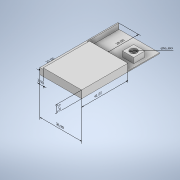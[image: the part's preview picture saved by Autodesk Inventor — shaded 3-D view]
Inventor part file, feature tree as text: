
AUTODESK INVENTOR PART (.ipt)
format: ipt  version: 2020 (Build 240168000, 168)  size: 172,032 bytes
history: native  units: mm
features: other x8, sketch x7, extrude x5, hole x1
ambient origin geometry x8: Origin, YZ Plane, XZ Plane, XY Plane, X Axis, Y Axis, Z Axis, Center Point
bodies: Solid1 (feature_tree)
feature tree (21):
  other  "Annotations"
  extrude  "Extrusion1"  Depth=69.0mm
  extrude  "Extrusion2"  Depth=34.0mm
  sketch  "Sketch4"  dims[d5=41.0mm d12=1.2mm d13=0.0mm]
  hole  "Hole1"  [1 undecoded]
  extrude  "Extrusion3"  Depth=54.15mm
  extrude  "Extrusion4"  Depth=10.0mm
  extrude  "Extrusion5"  Depth=28.0mm
  sketch  "Sketch1"  dims[d0=38.65mm d1=69.0mm]
  sketch  "Sketch3"  dims[d2=5.5mm d3=0.0mm d4=34.0mm]
  sketch  "Sketch5"  dims[d20=8.06mm d21=54.15mm]
  sketch  "Sketch6"  dims[d22=3.5mm d23=6.0mm d24=6.0mm d25=2.3mm d26=90.0deg d27=10.5mm d28=20.594885mm d32=10.0mm]
  sketch  "Sketch7"  dims[d33=10.0mm d37=28.0mm]
  sketch  "Sketch8"  dims[d38=4.75mm d39=0.0mm d40=30.0mm d41=25.0mm d42=5.75mm d43=0.0mm d49=1.75mm d50=0.0mm d10=10.0mm d11=6.7mm d14=0.0mm d15=10.0mm d16=2.9mm d17=0.0mm d18=10.0mm d19=36.9mm d29=0.0mm d30=10.0mm d31=41.0mm d34=1.687773mm d35=8.297323mm d36=28.0mm d44=0.0mm d45=10.0mm d46=25.0mm d47=40.77974mm d48=6.0mm d9=0.0mm d51=0.5mm d52=0.872665mm]
  other  "Linear Dimension 2"
  other  "Linear Dimension 3"
  other  "Linear Dimension 4"
  other  "Linear Dimension 5"
  other  "Linear Dimension 6"
  other  "Linear Dimension 7"
  other  "Diameter Dimension 1"
note: 1 required parameter value undecoded (feature->parameter linkage not recoverable at this tier; creation-order binding heuristic only, values carry confidence <= 0.55)
